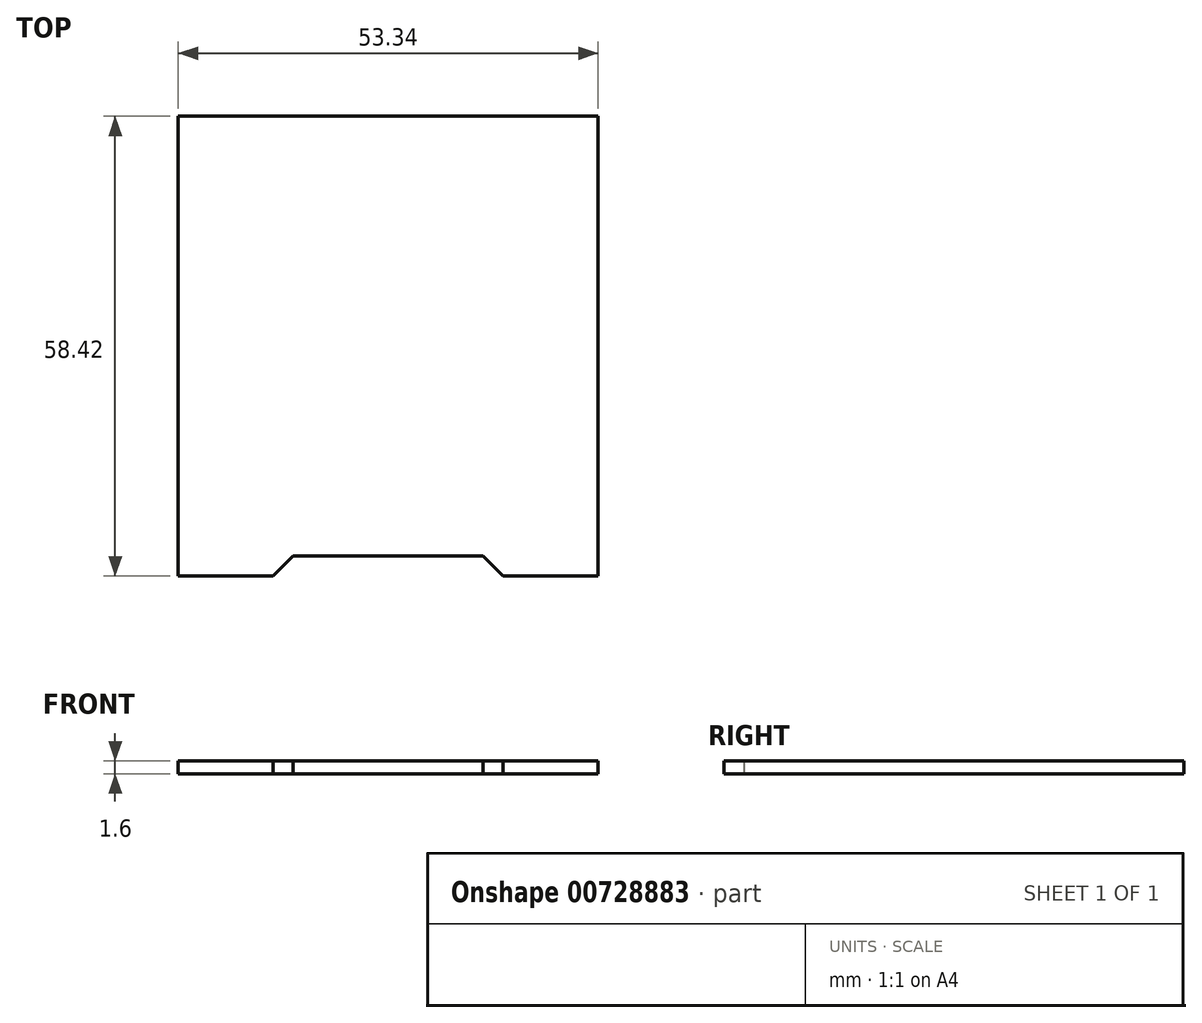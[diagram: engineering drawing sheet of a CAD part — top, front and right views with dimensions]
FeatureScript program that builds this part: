
annotation { "Feature Type Name" : "Feature", "Feature Type Description" : "" }
export const myFeature = defineFeature(function(context is Context, id is Id, definition is map)
    precondition{}
    {
        {
            var Q0;
            Q0=qCreatedBy(makeId("Top.planeOp"),FACE);
            var sketch = newSketch(context, id + "F0", { "sketchPlane" : qUnion([Q0])});
            skLineSegment(sketch, "E0.bottom", {"start": v(0, 0) * mm, "end": v(53.34, 0) * mm});
            skLineSegment(sketch, "E0.top", {"start": v(0, 58.42) * mm, "end": v(53.34, 58.42) * mm});
            skLineSegment(sketch, "E0.left", {"start": v(0, 0) * mm, "end": v(0, 58.42) * mm});
            skLineSegment(sketch, "E0.right", {"start": v(53.34, 0) * mm, "end": v(53.34, 58.42) * mm});
            skLineSegment(sketch, "E1", {"start": v(12.06, 0) * mm, "end": v(14.6, 2.54) * mm});
            skLineSegment(sketch, "E2", {"start": v(14.6, 2.54) * mm, "end": v(38.74, 2.54) * mm});
            skLineSegment(sketch, "E3", {"start": v(38.74, 2.54) * mm, "end": v(41.28, 0) * mm});
            skSolve(sketch);
        }
        {
            var Q0;
            Q0=makeQuery(id+"F0.imprint","IMPRINT",FACE,{"disambiguationData":[TD([[makeQuery(id+"F0.imprint","IMPRINT",EDGE,{"derivedFrom":sQuery(id+"F0.wireOp",EDGE,"E0.top")}),-1.0]])]});
            extrude(context, id + "F1", {"entities" : qUnion([Q0]), "depth" : 1.6 * mm, "offsetDistance" : 25 * mm});
        }
    });
